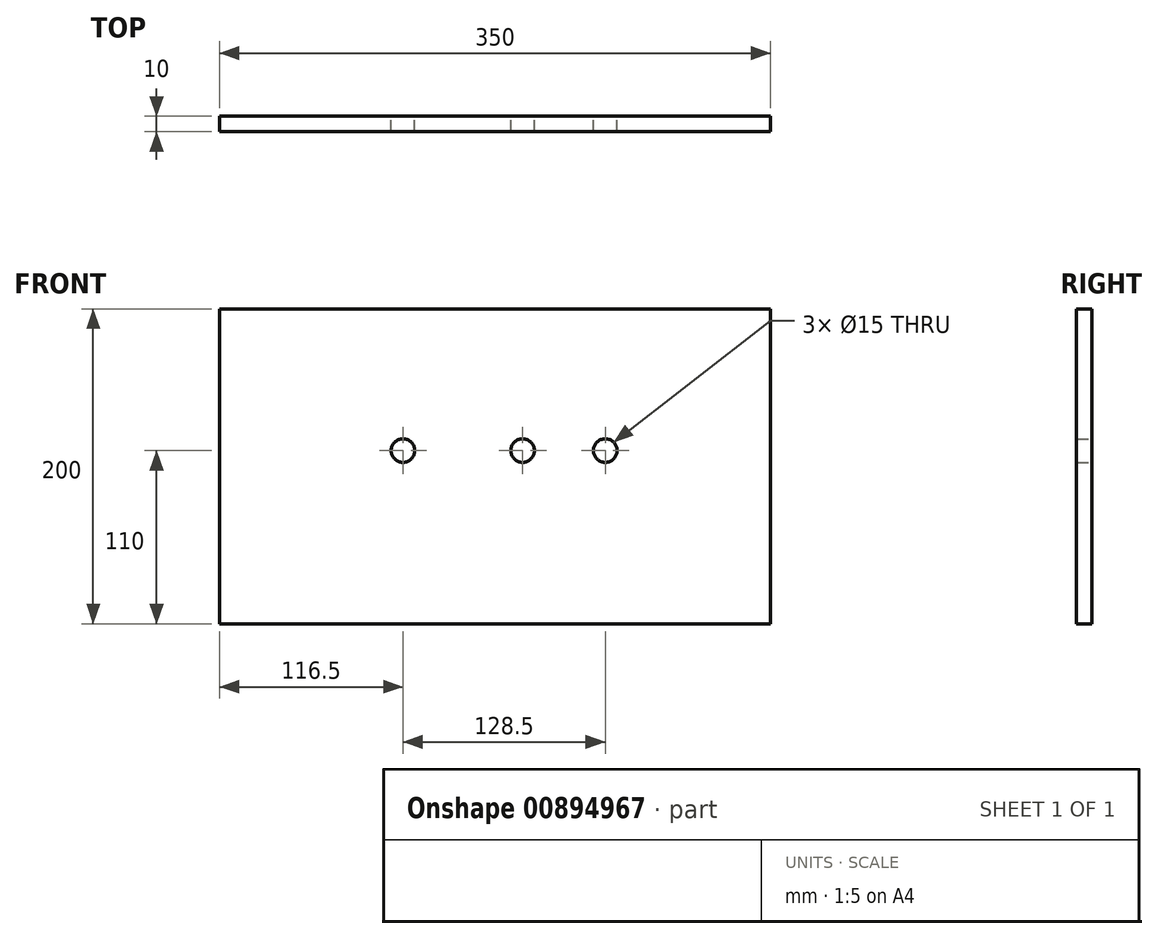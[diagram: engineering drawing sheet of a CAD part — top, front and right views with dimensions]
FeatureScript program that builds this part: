
annotation { "Feature Type Name" : "Feature", "Feature Type Description" : "" }
export const myFeature = defineFeature(function(context is Context, id is Id, definition is map)
    precondition{}
    {
        {
            var Q0;
            Q0=qCreatedBy(makeId("Front.planeOp"),FACE);
            var sketch = newSketch(context, id + "F0", { "sketchPlane" : qUnion([Q0])});
            skLineSegment(sketch, "E0.bottom", {"start": v(-175, 100) * mm, "end": v(175, 100) * mm});
            skLineSegment(sketch, "E0.top", {"start": v(-175, -100) * mm, "end": v(175, -100) * mm});
            skLineSegment(sketch, "E0.left", {"start": v(-175, 100) * mm, "end": v(-175, -100) * mm});
            skLineSegment(sketch, "E0.right", {"start": v(175, 100) * mm, "end": v(175, -100) * mm});
            skPoint(sketch, "E0.middle", {"position": v(0, 0) * mm});
            skCircle(sketch, "E1", {"center": v(70, 10) * mm, "radius": 7.5 * mm});
            skCircle(sketch, "E2", {"center": v(17.5, 10) * mm, "radius": 7.5 * mm});
            skCircle(sketch, "E3", {"center": v(-58.5, 10) * mm, "radius": 7.5 * mm});
            skSolve(sketch);
        }
        {
            var Q0;
            Q0=makeQuery(id+"F0.imprint","IMPRINT",FACE,{"disambiguationData":[TD([[makeQuery(id+"F0.imprint","IMPRINT",EDGE,{"derivedFrom":sQuery(id+"F0.wireOp",EDGE,"E0.bottom")}),-1.0]])]});
            extrude(context, id + "F1", {"entities" : qUnion([Q0]), "depth" : 10 * mm, "offsetDistance" : 25.4 * mm});
        }
    });
